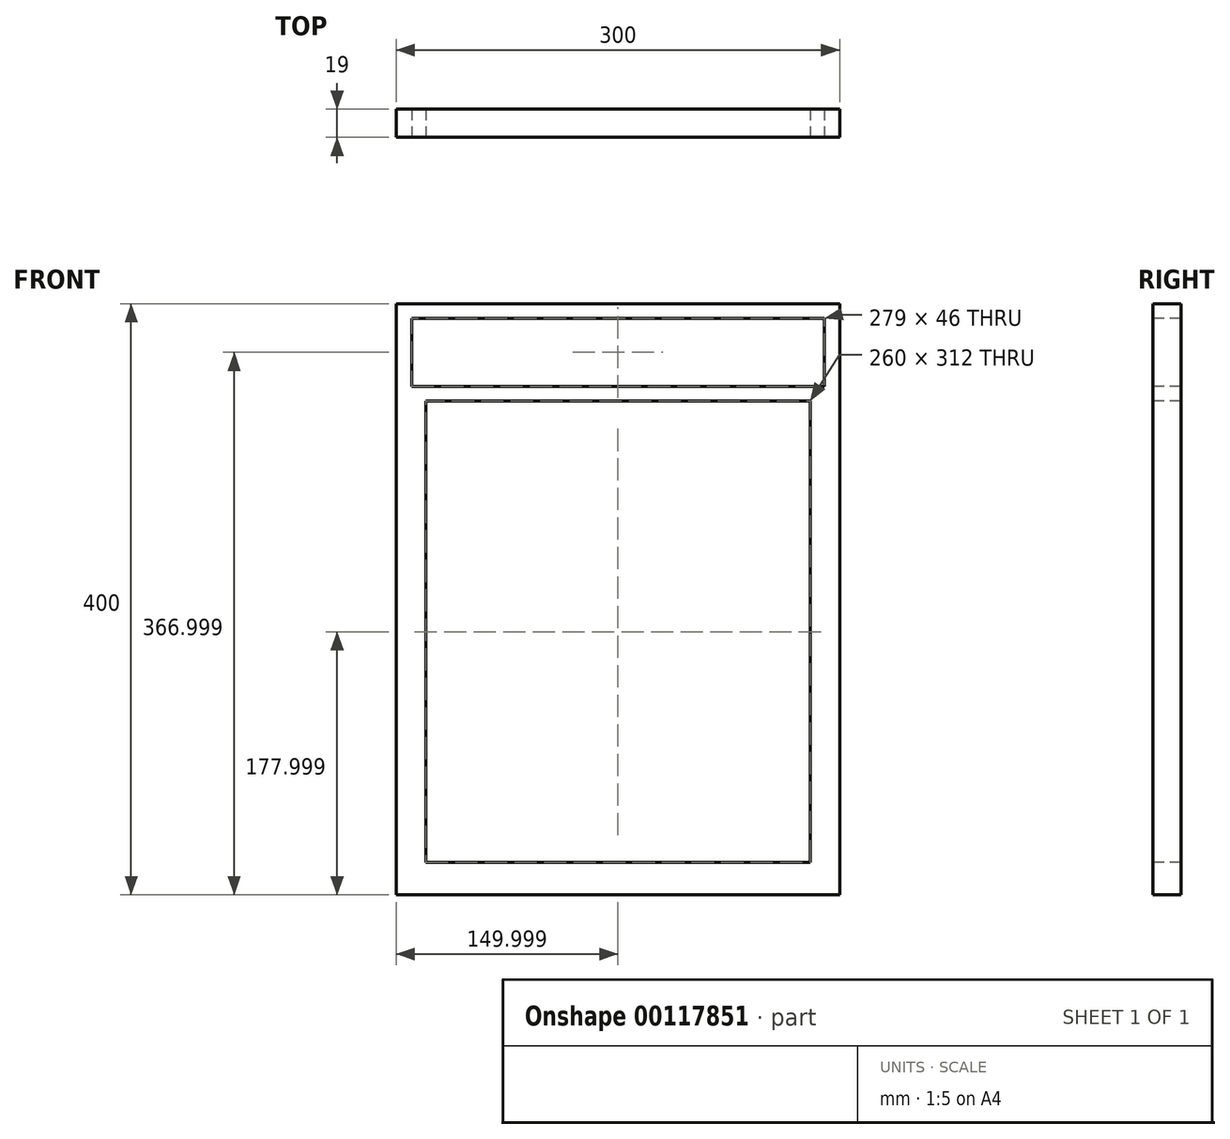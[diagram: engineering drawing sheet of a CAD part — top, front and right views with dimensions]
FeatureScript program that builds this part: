
annotation { "Feature Type Name" : "Feature", "Feature Type Description" : "" }
export const myFeature = defineFeature(function(context is Context, id is Id, definition is map)
    precondition{}
    {
        {
            var Q0;
            Q0=qCreatedBy(makeId("Front.planeOp"),FACE);
            var sketch = newSketch(context, id + "F0", { "sketchPlane" : qUnion([Q0])});
            skLineSegment(sketch, "E0.bottom", {"start": v(-165.58, 178.87) * mm, "end": v(134.42, 178.87) * mm});
            skLineSegment(sketch, "E0.top", {"start": v(-165.58, -221.13) * mm, "end": v(134.42, -221.13) * mm});
            skLineSegment(sketch, "E0.left", {"start": v(-165.58, 178.87) * mm, "end": v(-165.58, -221.13) * mm});
            skLineSegment(sketch, "E0.right", {"start": v(134.42, 178.87) * mm, "end": v(134.42, -221.13) * mm});
            skSolve(sketch);
        }
        {
            var Q0;
            Q0 = qSketchRegion(id + "F0", true);
            extrude(context, id + "F1", {"entities" : qUnion([Q0]), "depth" : 19 * mm});
        }
        {
            var Q0;
            Q0=makeQuery(id+"F1.opExtrude","CAP_FACE",FACE,{"disambiguationData":[OSD([sQuery(id+"F0.wireOp",EDGE,"E0.bottom"),sQuery(id+"F0.wireOp",EDGE,"E0.top"),sQuery(id+"F0.wireOp",EDGE,"E0.left"),sQuery(id+"F0.wireOp",EDGE,"E0.right")])],"isStart":false});
            var sketch = newSketch(context, id + "F2", { "sketchPlane" : qUnion([Q0])});
            skLineSegment(sketch, "E1.bottom", {"start": v(-155.08, 168.87) * mm, "end": v(123.92, 168.87) * mm});
            skLineSegment(sketch, "E1.top", {"start": v(-155.08, 122.87) * mm, "end": v(123.92, 122.87) * mm});
            skLineSegment(sketch, "E1.left", {"start": v(-155.08, 168.87) * mm, "end": v(-155.08, 122.87) * mm});
            skLineSegment(sketch, "E1.right", {"start": v(123.92, 168.87) * mm, "end": v(123.92, 122.87) * mm});
            skSolve(sketch);
        }
        {
            var Q0;
            Q0 = qSketchRegion(id + "F2", true);
            extrude(context, id + "F3", {"entities" : qUnion([Q0]), "operationType" : NewBodyOperationType.REMOVE, "oppositeDirection" : true, "depth" : 19 * mm});
        }
        {
            var Q0;
            Q0=makeQuery(id+"F1.opExtrude","CAP_FACE",FACE,{"disambiguationData":[OSD([sQuery(id+"F0.wireOp",EDGE,"E0.bottom"),sQuery(id+"F0.wireOp",EDGE,"E0.top"),sQuery(id+"F0.wireOp",EDGE,"E0.left"),sQuery(id+"F0.wireOp",EDGE,"E0.right")])],"isStart":false});
            var sketch = newSketch(context, id + "F4", { "sketchPlane" : qUnion([Q0])});
            skLineSegment(sketch, "E2.bottom", {"start": v(-145.58, 112.87) * mm, "end": v(114.42, 112.87) * mm});
            skLineSegment(sketch, "E2.top", {"start": v(-145.58, -199.13) * mm, "end": v(114.42, -199.13) * mm});
            skLineSegment(sketch, "E2.left", {"start": v(-145.58, 112.87) * mm, "end": v(-145.58, -199.13) * mm});
            skLineSegment(sketch, "E2.right", {"start": v(114.42, 112.87) * mm, "end": v(114.42, -199.13) * mm});
            skSolve(sketch);
        }
        {
            var Q0;
            Q0 = qSketchRegion(id + "F4", true);
            extrude(context, id + "F5", {"entities" : qUnion([Q0]), "operationType" : NewBodyOperationType.REMOVE, "oppositeDirection" : true, "depth" : 19 * mm});
        }
    });
